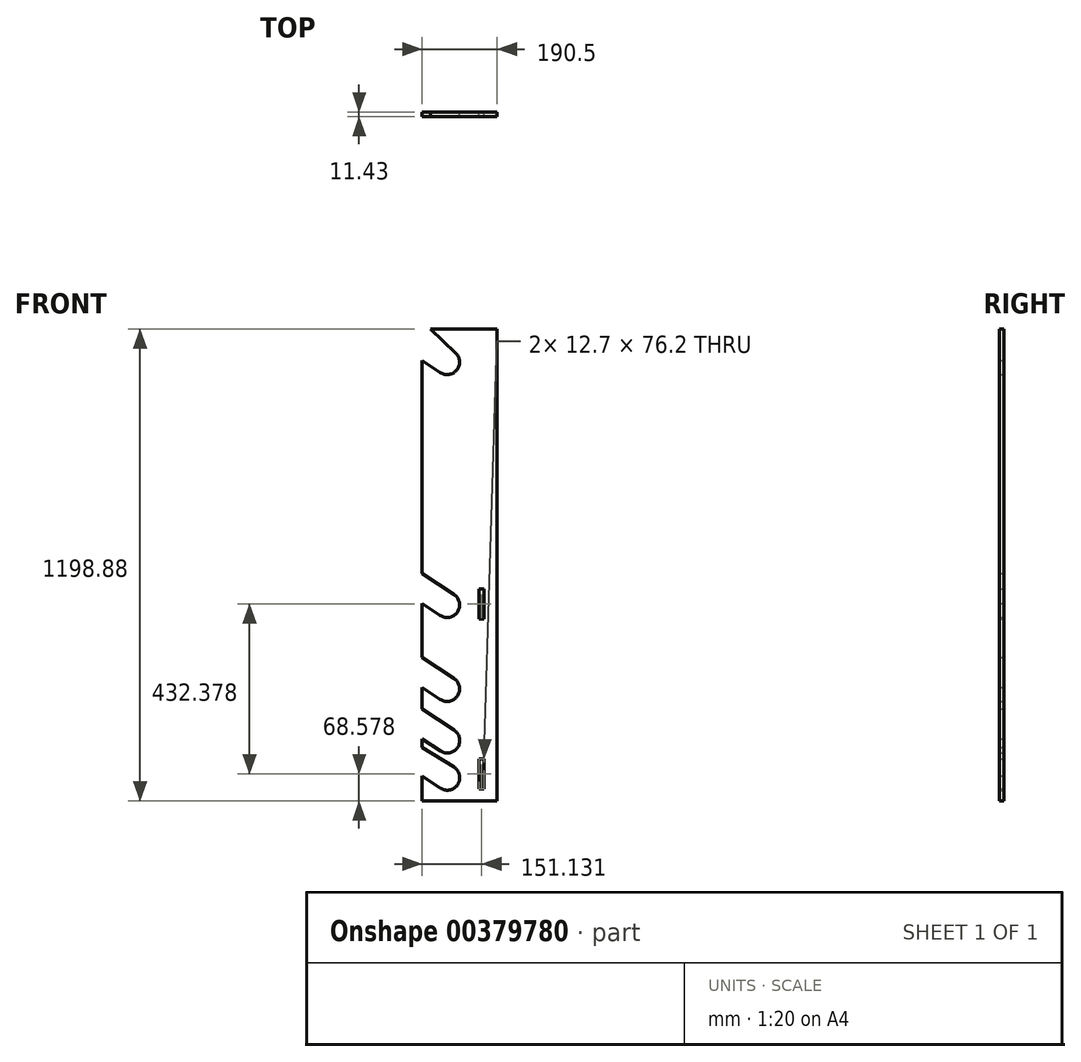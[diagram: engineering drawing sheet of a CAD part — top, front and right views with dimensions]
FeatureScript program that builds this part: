
annotation { "Feature Type Name" : "Feature", "Feature Type Description" : "" }
export const myFeature = defineFeature(function(context is Context, id is Id, definition is map)
    precondition{}
    {
        {
            var Q0;
            Q0=qCreatedBy(makeId("Front.planeOp"),FACE);
            var sketch = newSketch(context, id + "F0", { "sketchPlane" : qUnion([Q0])});
            skLineSegment(sketch, "E0.bottom", {"start": v(-82.66, 487.6) * mm, "end": v(86.44, 487.6) * mm});
            skLineSegment(sketch, "E0.top", {"start": v(-104.06, -731.6) * mm, "end": v(86.44, -731.6) * mm});
            skLineSegment(sketch, "E0.right", {"start": v(86.44, 487.6) * mm, "end": v(86.44, -731.6) * mm});
            skLineSegment(sketch, "E1", {"start": v(-104.06, -553.68) * mm, "end": v(-57.87, -584.32) * mm});
            skLineSegment(sketch, "E2", {"start": v(-104.06, -477.48) * mm, "end": v(-22.77, -531.4) * mm});
            skArc(sketch, "E3", {"start": v(-57.87, -584.32) * mm, "mid": v(-13.86, -575.42) * mm, "end": v(-22.77, -531.4) * mm});
            skLineSegment(sketch, "E4", {"start": v(-104.06, -346.66) * mm, "end": v(-23.12, -400.34) * mm});
            skLineSegment(sketch, "E5", {"start": v(-104.06, -422.86) * mm, "end": v(-58.22, -453.26) * mm});
            skArc(sketch, "E6", {"start": v(-58.22, -453.26) * mm, "mid": v(-14.21, -444.35) * mm, "end": v(-23.12, -400.34) * mm});
            skLineSegment(sketch, "E7", {"start": v(-104.06, -209.42) * mm, "end": v(-58.1, -239.9) * mm});
            skLineSegment(sketch, "E8", {"start": v(-104.06, -133.22) * mm, "end": v(-23, -186.98) * mm});
            skArc(sketch, "E9", {"start": v(-58.1, -239.9) * mm, "mid": v(-14.1, -231) * mm, "end": v(-23, -186.98) * mm});
            skPoint(sketch, "E10.orphan", {"position": v(-91.17, -217.97) * mm});
            skLineSegment(sketch, "E11", {"start": v(-104.06, 407.74) * mm, "end": v(-104.06, -133.22) * mm});
            skLineSegment(sketch, "E12", {"start": v(-104.06, -209.42) * mm, "end": v(-104.06, -346.66) * mm});
            skLineSegment(sketch, "E13", {"start": v(-104.06, -422.86) * mm, "end": v(-104.06, -477.48) * mm});
            skPoint(sketch, "E14.endSnap0", {"position": v(-10.42, 429.54) * mm});
            skArc(sketch, "E15", {"start": v(-58.22, 377.32) * mm, "mid": v(-15.85, 383.98) * mm, "end": v(-18.77, 426.77) * mm});
            skLineSegment(sketch, "E16", {"start": v(-58.22, 377.32) * mm, "end": v(-104.06, 407.74) * mm});
            skLineSegment(sketch, "E17", {"start": v(-18.77, 426.77) * mm, "end": v(-82.66, 487.6) * mm});
            skArc(sketch, "E18", {"start": v(-57.87, -678.81) * mm, "mid": v(-13.6, -669.5) * mm, "end": v(-23.57, -625.38) * mm});
            skLineSegment(sketch, "E19.trimOffspring", {"start": v(-104.06, -553.68) * mm, "end": v(-104.06, -575.43) * mm});
            skLineSegment(sketch, "E20", {"start": v(-57.87, -678.81) * mm, "end": v(-104.06, -648.17) * mm});
            skLineSegment(sketch, "E21", {"start": v(-23.57, -625.38) * mm, "end": v(-104.06, -575.43) * mm});
            skLineSegment(sketch, "E22.trimOffspring", {"start": v(-104.06, -648.17) * mm, "end": v(-104.06, -731.6) * mm});
            skLineSegment(sketch, "E23.bottom", {"start": v(40.72, -680.8) * mm, "end": v(53.42, -680.8) * mm});
            skLineSegment(sketch, "E23.top", {"start": v(40.72, -604.6) * mm, "end": v(53.42, -604.6) * mm});
            skLineSegment(sketch, "E23.left", {"start": v(40.72, -680.8) * mm, "end": v(40.72, -604.6) * mm});
            skLineSegment(sketch, "E23.right", {"start": v(53.42, -680.8) * mm, "end": v(53.42, -604.6) * mm});
            skLineSegment(sketch, "E24.bottom", {"start": v(40.72, -172.22) * mm, "end": v(53.42, -172.22) * mm});
            skLineSegment(sketch, "E24.top", {"start": v(40.72, -248.42) * mm, "end": v(53.42, -248.42) * mm});
            skLineSegment(sketch, "E24.left", {"start": v(40.72, -172.22) * mm, "end": v(40.72, -248.42) * mm});
            skLineSegment(sketch, "E24.right", {"start": v(53.42, -172.22) * mm, "end": v(53.42, -248.42) * mm});
            skPoint(sketch, "E25.endSnap0", {"position": v(-104.06, -689.89) * mm});
            skLineSegment(sketch, "E26", {"start": v(47.07, -711.28) * mm, "end": v(86.44, -711.28) * mm});
            skLineSegment(sketch, "E27", {"start": v(47.07, -711.28) * mm, "end": v(-104.06, -711.28) * mm});
            skLineSegment(sketch, "E28", {"start": v(113.2, -711.28) * mm, "end": v(113.2, -731.63) * mm});
            skSolve(sketch);
        }
        {
            var Q0;
            Q0=makeQuery(id+"F0.imprint","IMPRINT",FACE,{"disambiguationData":[TD([[makeQuery(id+"F0.imprint","IMPRINT",EDGE,{"derivedFrom":sQuery(id+"F0.wireOp",EDGE,"ea1434a7-de2b-4940-9681-53a8eaaeeed7.bottom")}),-1.0]])]});
            var Q1;
            {var subQ4=sQuery(id+"F0.wireOp",EDGE,"E0.bottom");Q1=makeQuery(id+"F0.imprint","IMPRINT",FACE,{"disambiguationData":[TD([[makeQuery(id+"F0.imprint","IMPRINT",EDGE,{"derivedFrom":subQ4}),-1.0]])]});}
            extrude(context, id + "F1", {"entities" : qUnion([Q0, Q1]), "depth" : 11.43 * mm});
        }
    });
